# Revit family: Draining Ball Valve_DN10-15_RFA
name_source: partatom
category: Pipe Accessories
units: mm (PartAtom-declared; Revit-internal decimal feet)

## family parameters
Always vertical = Yes
Cut with Voids When Loaded = No
Part Type = Valve - Breaks Into
Round Connector Dimension = Use Diameter
Shared = No
Work Plane-Based = No

## types (2) — shared parameters
Description = Draining Ball Valve
L4 = 2 mm  [stored 0.00656168 ft]
LOD 200 = No
LOD 350 = Yes
Manufacturer = Danfoss
URL = https://store.danfoss.com
Valve Body Material = Danfoss Brass

## per-type parameters (varying)
| type | D | D1 | D2 | D3 | D4 | H | H1 | L | L1 | L2 | L3 | L5 | L6 | L7 | L8 | Model | Model Type |
| Draining Ball Valve_DN10_065B7802 | 10 mm  [stored 0.0328084 ft] | 12 mm  [stored 0.0393701 ft] | 14 mm  [stored 0.0459318 ft] | 16 mm  [stored 0.0524934 ft] | 15 mm  [stored 0.0492126 ft] | 36 mm  [stored 0.11811 ft] | 12 mm  [stored 0.0393701 ft] | 52 mm | 20 mm  [stored 0.0656168 ft] | 10 mm  [stored 0.0328084 ft] | 5 mm  [stored 0.0164042 ft] | 6 mm  [stored 0.019685 ft] | 8 mm  [stored 0.0262467 ft] | 43 mm  [stored 0.141076 ft] | 20 mm  [stored 0.0656168 ft] | 065B7802 | Draining Ball Valve_DN10 |
| Draining Ball Valve_DN15_065B7801 | 15 mm  [stored 0.0492126 ft] | 20 mm  [stored 0.0656168 ft] | 24 mm  [stored 0.0787402 ft] | 28 mm  [stored 0.0918635 ft] | 23 mm  [stored 0.0754593 ft] | 52 mm | 20 mm  [stored 0.0656168 ft] | 69 mm  [stored 0.226378 ft] | 27 mm  [stored 0.0885827 ft] | 17 mm | 7 mm  [stored 0.0229659 ft] | 8 mm  [stored 0.0262467 ft] | 10 mm  [stored 0.0328084 ft] | 50 mm  [stored 0.164042 ft] | 22 mm  [stored 0.0721785 ft] | 065B7801 | Draining Ball Valve_DN15 |

note: [stored X ft] marks values corroborated as IEEE doubles in the binary element streams (Revit-internal decimal feet)

## geometry (parser evidence)
native form markers: Sweep x6
no freeform markers — native parametric forms only
